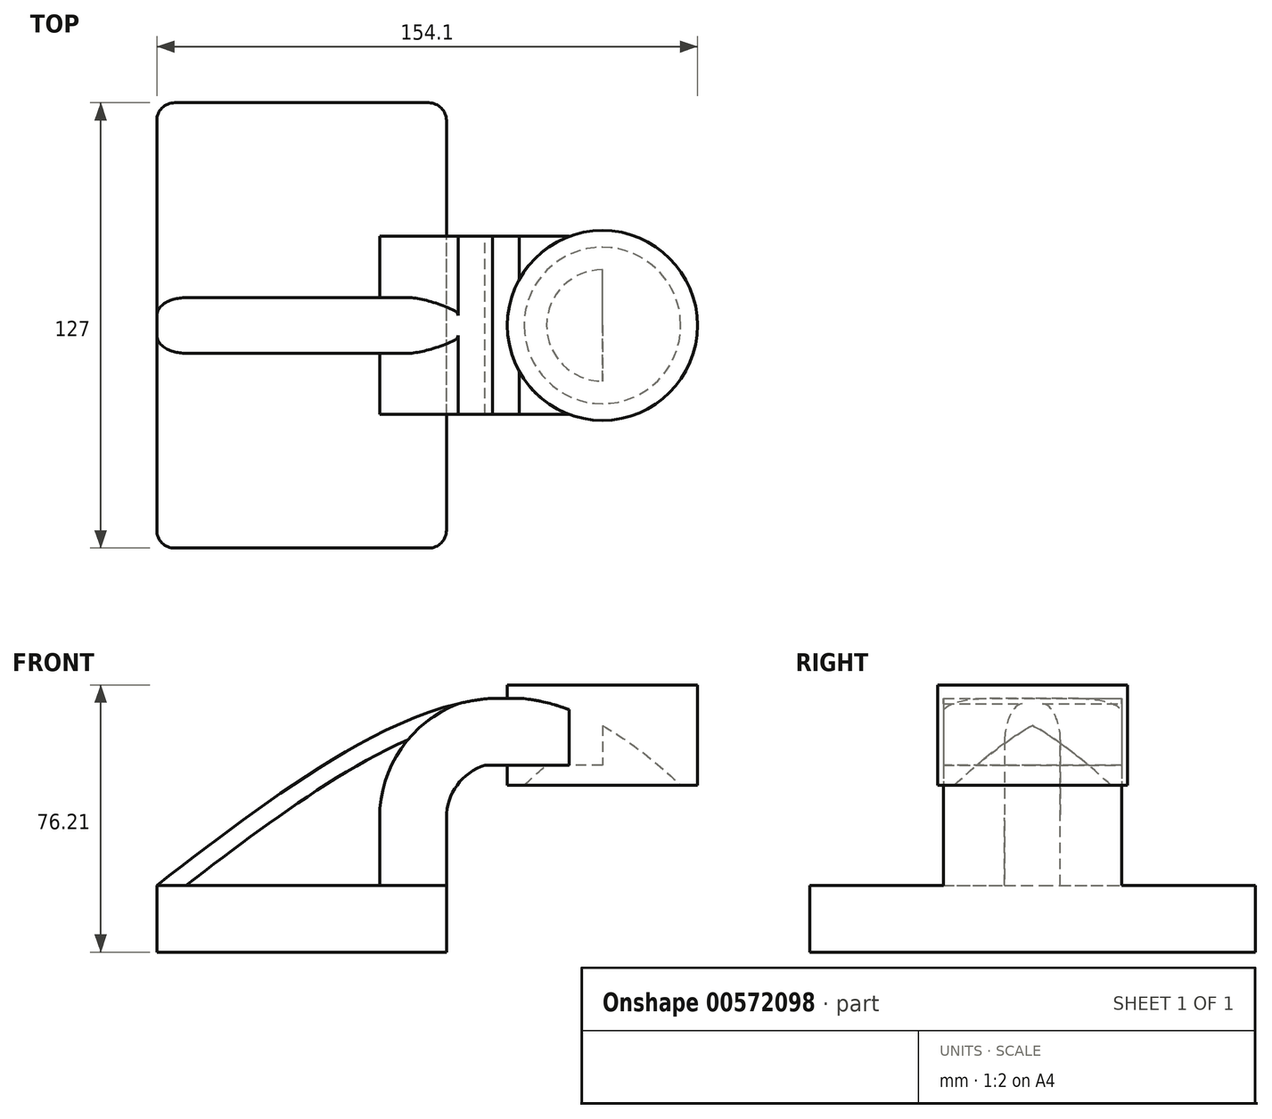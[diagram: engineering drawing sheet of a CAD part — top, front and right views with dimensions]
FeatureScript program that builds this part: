
annotation { "Feature Type Name" : "Feature", "Feature Type Description" : "" }
export const myFeature = defineFeature(function(context is Context, id is Id, definition is map)
    precondition{}
    {
        {
            var Q0;
            Q0=qCreatedBy(makeId("Front.planeOp"),FACE);
            var sketch = newSketch(context, id + "F0", { "sketchPlane" : qUnion([Q0])});
            skLineSegment(sketch, "E0.bottom", {"start": v(41.28, 9.53) * mm, "end": v(-41.27, 9.53) * mm});
            skLineSegment(sketch, "E0.top", {"start": v(41.28, -9.53) * mm, "end": v(-41.27, -9.53) * mm});
            skLineSegment(sketch, "E0.left", {"start": v(41.28, 9.53) * mm, "end": v(41.28, -9.52) * mm});
            skLineSegment(sketch, "E0.right", {"start": v(-41.27, 9.53) * mm, "end": v(-41.27, -9.53) * mm});
            skPoint(sketch, "E0.middle", {"position": v(0, 0) * mm});
            skLineSegment(sketch, "E1.bottom", {"start": v(62.02, 66.68) * mm, "end": v(112.82, 66.68) * mm});
            skLineSegment(sketch, "E1.top", {"start": v(62.02, 38.1) * mm, "end": v(112.82, 38.1) * mm});
            skLineSegment(sketch, "E1.left", {"start": v(62.02, 66.68) * mm, "end": v(62.02, 38.1) * mm});
            skLineSegment(sketch, "E1.right", {"start": v(112.82, 66.68) * mm, "end": v(112.82, 38.1) * mm});
            skPoint(sketch, "E2.startSnap0", {"position": v(62.02, 52.39) * mm});
            skLineSegment(sketch, "E3", {"start": v(41.28, 9.53) * mm, "end": v(41.28, 28.71) * mm});
            skArc(sketch, "E4", {"start": v(52.26, 43.82) * mm, "mid": v(44.31, 38.05) * mm, "end": v(41.28, 28.71) * mm});
            skLineSegment(sketch, "E5", {"start": v(52.26, 43.82) * mm, "end": v(85.73, 43.82) * mm});
            skLineSegment(sketch, "E6.0", {"start": v(54.47, 62.87) * mm, "end": v(85.73, 62.87) * mm});
            skArc(sketch, "E6.1", {"start": v(44.69, 61.34) * mm, "mid": v(28.38, 48.52) * mm, "end": v(22.23, 28.71) * mm});
            skLineSegment(sketch, "E6.2", {"start": v(22.23, 9.53) * mm, "end": v(22.23, 28.71) * mm});
            skLineSegment(sketch, "E7", {"start": v(85.73, 62.87) * mm, "end": v(85.73, 38.1) * mm});
            skLineSegment(sketch, "E8", {"start": v(85.73, 38.1) * mm, "end": v(85.73, 66.68) * mm});
            skFitSpline(sketch, "E9", {"points": [v(-41.28, 9.53) * mm, v(62.02, 62.87) * mm, v(135.16, 9.53) * mm], "startDerivative": vector(204.65, 157.3) * mm, "endDerivative": vector(147.02, -164) * mm});
            skSolve(sketch);
        }
        {
            var Q0;
            Q0=makeQuery(id+"F0.imprint","IMPRINT",FACE,{"disambiguationData":[TD([[makeQuery(id+"F0.imprint","IMPRINT",EDGE,{"derivedFrom":sQuery(id+"F0.wireOp",EDGE,"E0.top")}),-1.0]])]});
            extrude(context, id + "F1", {"entities" : qUnion([Q0]), "endBound" : BoundingType.SYMMETRIC, "depth" : 127 * mm, "offsetDistance" : 25.4 * mm});
        }
        {
            var Q0;
            {var subQ4=sQuery(id+"F0.wireOp",EDGE,"E6.1");Q0=makeQuery(id+"F0.imprint","IMPRINT",FACE,{"disambiguationData":[TD([[makeQuery(id+"F0.imprint","IMPRINT",EDGE,{"derivedFrom":subQ4}),-1.0]])]});}
            extrude(context, id + "F2", {"entities" : qUnion([Q0]), "operationType" : NewBodyOperationType.ADD, "endBound" : BoundingType.SYMMETRIC, "depth" : 15.88 * mm, "offsetDistance" : 25.4 * mm});
        }
        {
            var Q0;
            {var subQ5=sQuery(id+"F0.wireOp",EDGE,"E3");Q0=makeQuery(id+"F0.imprint","IMPRINT",FACE,{"disambiguationData":[TD([[makeQuery(id+"F0.imprint","IMPRINT",EDGE,{"derivedFrom":subQ5}),1.0]])]});}
            var Q1;
            {var subQ0=sQuery(id+"F0.wireOp",EDGE,"E6.0");var subQ1=sQuery(id+"F0.wireOp",EDGE,"E1.left");var subQ2=makeQuery(id+"F0.imprint","INTERSECT",VERTEX,{"derivedFrom":[subQ1,subQ0]});Q1=makeQuery(id+"F0.imprint","IMPRINT",FACE,{"disambiguationData":[TD([[makeQuery(id+"F0.imprint","IMPRINT",EDGE,{"disambiguationData":[TD([[subQ2,-1.0]])],"derivedFrom":subQ1}),1.0]])]});}
            extrude(context, id + "F3", {"entities" : qUnion([Q0, Q1]), "operationType" : NewBodyOperationType.ADD, "endBound" : BoundingType.SYMMETRIC, "depth" : 50.8 * mm, "offsetDistance" : 25.4 * mm});
        }
        {
            var Q0;
            {var subQ0=sQuery(id+"F0.wireOp",EDGE,"E1.right");Q0=makeQuery(id+"F0.imprint","IMPRINT",FACE,{"disambiguationData":[TD([[makeQuery(id+"F0.imprint","IMPRINT",EDGE,{"derivedFrom":subQ0}),-1.0]])]});}
            var Q1;
            Q1=sQuery(id+"F0.wireOp",EDGE,"E8");
            revolve(context, id + "F4", {"operationType" : NewBodyOperationType.ADD, "entities" : qUnion([Q0]), "axis" : qUnion([Q1]), "revolveType" : RevolveType.FULL});
        }
        {
            var Q0;
            Q0=makeQuery(id+"F1.opExtrude","CAP_EDGE",EDGE,{"disambiguationData":[OSD([sQuery(id+"F0.wireOp",EDGE,"E0.left")])],"isStart":false});
            var Q1;
            Q1=makeQuery(id+"F1.opExtrude","CAP_EDGE",EDGE,{"disambiguationData":[OSD([sQuery(id+"F0.wireOp",EDGE,"E0.left")])],"isStart":true});
            var Q2;
            Q2=makeQuery(id+"F1.opExtrude","CAP_EDGE",EDGE,{"disambiguationData":[OSD([sQuery(id+"F0.wireOp",EDGE,"E0.right")])],"isStart":true});
            var Q3;
            Q3=makeQuery(id+"F1.opExtrude","CAP_EDGE",EDGE,{"disambiguationData":[OSD([sQuery(id+"F0.wireOp",EDGE,"E0.right")])],"isStart":false});
            var Q4;
            Q4=makeQuery(id+"F2.opExtrude","CAP_EDGE",EDGE,{"disambiguationData":[OSD([sQuery(id+"F0.wireOp",EDGE,"E9")])],"isStart":false});
            var Q5;
            Q5=makeQuery(id+"F2.opExtrude","CAP_EDGE",EDGE,{"disambiguationData":[OSD([sQuery(id+"F0.wireOp",EDGE,"E9")])],"isStart":true});
            fillet(context, id + "F5", {"entities" : qUnion([Q0, Q1, Q2, Q3, Q4, Q5]), "radius" : 5.08 * mm, "tangentPropagation" : true, "allowEdgeOverflow" : false});
        }
    });
